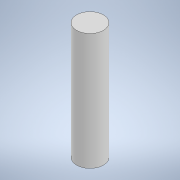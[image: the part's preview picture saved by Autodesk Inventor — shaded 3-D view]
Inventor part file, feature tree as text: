
AUTODESK INVENTOR PART (.ipt)
format: ipt  version: 2022 (Build 260153000, 153)  size: 93,184 bytes
history: native  units: mm
features: extrude x1, sketch x1
ambient origin geometry x8: Origin, YZ Plane, XZ Plane, XY Plane, X Axis, Y Axis, Z Axis, Center Point
bodies: Solide1 (feature_tree)
feature tree (2):
  extrude  "Extrusion1"  Depth=4.6mm
  sketch  "Esquisse1"
